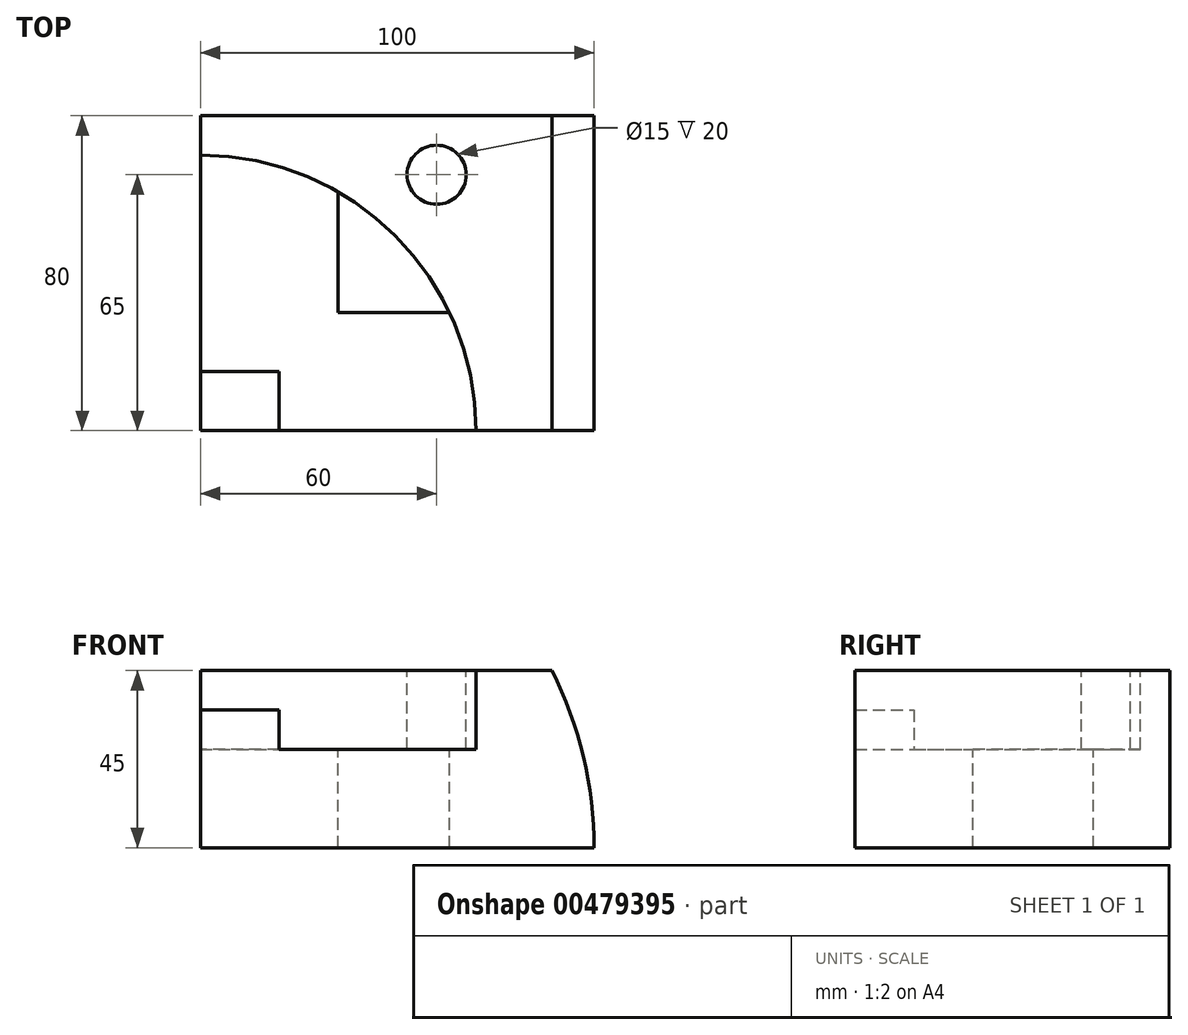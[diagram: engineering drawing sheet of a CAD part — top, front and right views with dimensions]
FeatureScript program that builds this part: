
annotation { "Feature Type Name" : "Feature", "Feature Type Description" : "" }
export const myFeature = defineFeature(function(context is Context, id is Id, definition is map)
    precondition{}
    {
        {
            var Q0;
            Q0=qCreatedBy(makeId("Front.planeOp"),FACE);
            var sketch = newSketch(context, id + "F0", { "sketchPlane" : qUnion([Q0])});
            skCircle(sketch, "E0", {"center": v(0, 0) * mm, "radius": 100 * mm});
            skSolve(sketch);
        }
        {
            var Q0;
            Q0 = qSketchRegion(id + "F0", true);
            extrude(context, id + "F1", {"entities" : qUnion([Q0]), "oppositeDirection" : true, "depth" : 80 * mm});
        }
        {
            var Q0;
            Q0=makeQuery(id+"F1.opExtrude","CAP_FACE",FACE,{"disambiguationData":[OSD([sQuery(id+"F0.wireOp",EDGE,"E0")])],"isStart":true});
            var sketch = newSketch(context, id + "F2", { "sketchPlane" : qUnion([Q0])});
            skArc(sketch, "E1", {"start": v(0, 100) * mm, "mid": v(-70.71, -70.71) * mm, "end": v(100, 0) * mm});
            skLineSegment(sketch, "E2", {"start": v(0, 100) * mm, "end": v(0, 0) * mm});
            skLineSegment(sketch, "E3", {"start": v(100, 0) * mm, "end": v(0, 0) * mm});
            skSolve(sketch);
        }
        {
            var Q0;
            Q0 = qSketchRegion(id + "F2", true);
            extrude(context, id + "F3", {"entities" : qUnion([Q0]), "operationType" : NewBodyOperationType.REMOVE, "endBound" : BoundingType.THROUGH_ALL, "oppositeDirection" : true, "depth" : 25 * mm});
        }
        {
            var Q0;
            Q0=makeQuery(id+"F1.opExtrude","CAP_FACE",FACE,{"disambiguationData":[OSD([sQuery(id+"F0.wireOp",EDGE,"E0")])],"isStart":true});
            var sketch = newSketch(context, id + "F4", { "sketchPlane" : qUnion([Q0])});
            skLineSegment(sketch, "E4.bottom", {"start": v(-23.34, 128.41) * mm, "end": v(127.02, 128.41) * mm});
            skLineSegment(sketch, "E4.top", {"start": v(-23.34, 45) * mm, "end": v(127.02, 45) * mm});
            skLineSegment(sketch, "E4.left", {"start": v(-23.34, 128.41) * mm, "end": v(-23.34, 45) * mm});
            skLineSegment(sketch, "E4.right", {"start": v(127.02, 128.41) * mm, "end": v(127.02, 45) * mm});
            skSolve(sketch);
        }
        {
            var Q0;
            Q0 = qSketchRegion(id + "F4", true);
            extrude(context, id + "F5", {"entities" : qUnion([Q0]), "operationType" : NewBodyOperationType.REMOVE, "endBound" : BoundingType.THROUGH_ALL, "oppositeDirection" : true, "depth" : 25 * mm});
        }
        {
            var Q0;
            Q0=makeQuery(id+"F5.boolean.opBoolean","COPY",FACE,{"derivedFrom":makeQuery(id+"F5.opExtrude","SWEPT_FACE",FACE,{"disambiguationData":[OSD([sQuery(id+"F4.wireOp",EDGE,"E4.top")])]})});
            var sketch = newSketch(context, id + "F6", { "sketchPlane" : qUnion([Q0])});
            skCircle(sketch, "E5", {"center": v(60, 65) * mm, "radius": 7.5 * mm});
            skCircle(sketch, "E6", {"center": v(0, 0) * mm, "radius": 70 * mm});
            skSolve(sketch);
        }
        {
            var Q0;
            Q0 = qSketchRegion(id + "F6", true);
            extrude(context, id + "F7", {"entities" : qUnion([Q0]), "operationType" : NewBodyOperationType.REMOVE, "oppositeDirection" : true, "depth" : 20 * mm});
        }
        {
            var Q0;
            Q0=makeQuery(id+"F7.boolean.opBoolean","COPY",FACE,{"derivedFrom":makeQuery(id+"F7.opExtrude","CAP_FACE",FACE,{"disambiguationData":[OSD([sQuery(id+"F6.wireOp",EDGE,"E6")])],"isStart":false})});
            var sketch = newSketch(context, id + "F8", { "sketchPlane" : qUnion([Q0])});
            skLineSegment(sketch, "E7", {"start": v(35, 69.01) * mm, "end": v(35, 30) * mm});
            skLineSegment(sketch, "E8", {"start": v(35, 30) * mm, "end": v(70, 30) * mm});
            skSolve(sketch);
        }
        {
            var Q0;
            {var subQ0=sQuery(id+"F8.wireOp",EDGE,"E8");var subQ1=sQuery(id+"F8.wireOp",EDGE,"E7");var subQ2=makeQuery(id+"F8.imprint","INTERSECT",VERTEX,{"derivedFrom":[subQ1,subQ0]});Q0=makeQuery(id+"F8.imprint","IMPRINT",FACE,{"disambiguationData":[TD([[makeQuery(id+"F8.imprint","IMPRINT",EDGE,{"disambiguationData":[TD([[subQ2,1.0]])],"derivedFrom":subQ1}),1.0]])]});}
            extrude(context, id + "F9", {"entities" : qUnion([Q0]), "operationType" : NewBodyOperationType.REMOVE, "endBound" : BoundingType.THROUGH_ALL, "oppositeDirection" : true, "depth" : 25 * mm});
        }
        {
            var Q0;
            Q0=makeQuery(id+"F7.boolean.opBoolean","COPY",FACE,{"derivedFrom":makeQuery(id+"F7.opExtrude","CAP_FACE",FACE,{"disambiguationData":[OSD([sQuery(id+"F6.wireOp",EDGE,"E6")])],"isStart":false})});
            var sketch = newSketch(context, id + "F10", { "sketchPlane" : qUnion([Q0])});
            skLineSegment(sketch, "E9.bottom", {"start": v(0, 0) * mm, "end": v(20, 0) * mm});
            skLineSegment(sketch, "E9.top", {"start": v(0, 15) * mm, "end": v(20, 15) * mm});
            skLineSegment(sketch, "E9.left", {"start": v(0, 0) * mm, "end": v(0, 15) * mm});
            skLineSegment(sketch, "E9.right", {"start": v(20, 0) * mm, "end": v(20, 15) * mm});
            skSolve(sketch);
        }
        {
            var Q0;
            Q0 = qSketchRegion(id + "F10", true);
            extrude(context, id + "F11", {"entities" : qUnion([Q0]), "operationType" : NewBodyOperationType.ADD, "depth" : 10 * mm});
        }
    });
